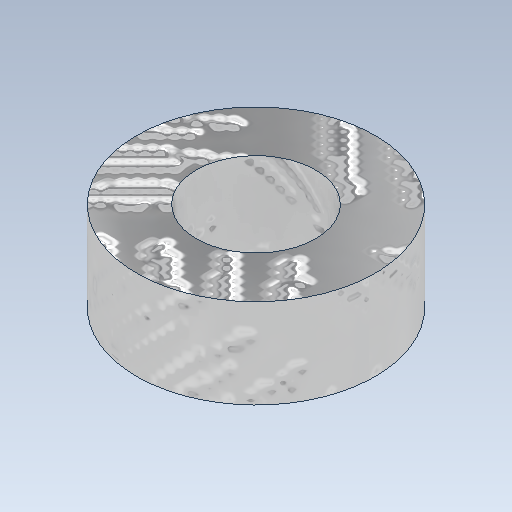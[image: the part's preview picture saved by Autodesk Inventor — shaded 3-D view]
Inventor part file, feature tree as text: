
AUTODESK INVENTOR PART (.ipt)
format: ipt  version: 2020.3 (Build 243373000, 373)  size: 164,864 bytes
history: native  units: mm
features: other x1, extrude x1, sketch x1
ambient origin geometry x8: Origin, YZ Plane, XZ Plane, XY Plane, X Axis, Y Axis, Z Axis, Center Point
bodies: Body1 (feature_tree)
feature tree (3):
  other  "ソリッド1"
  extrude  "押し出し1"  Depth=8.0mm
  sketch  "スケッチ1"
